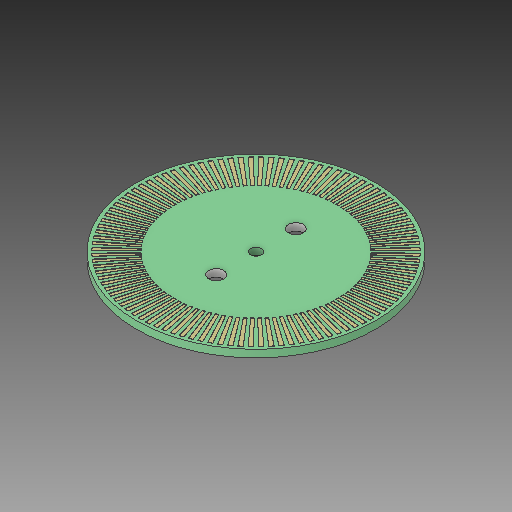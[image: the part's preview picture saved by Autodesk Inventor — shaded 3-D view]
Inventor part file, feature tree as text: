
AUTODESK INVENTOR PART (.ipt)
format: ipt  version: 2018.2 (Build 222227000, 227)  size: 907,264 bytes
history: native  units: mm
features: sketch x3, extrude x2, pattern_circular x1, plane x1, mirror x1, hole x1
ambient origin geometry x8: Origin, YZ Plane, XZ Plane, XY Plane, X Axis, Y Axis, Z Axis, Center Point
bodies: Solid1 (feature_tree)
feature tree (9):
  extrude  "Extrusion1"  Depth=2.23mm
  extrude  "Extrusion2"  Depth=1.5mm
  pattern_circular  "Circular Pattern1"  [2 undecoded]
  plane  "Work Plane1"
  mirror  "Mirror1"
  hole  "Hole1"  [1 undecoded]
  sketch  "Sketch1"  dims[d0=48.0mm d1=2.23mm]
  sketch  "Sketch2"  dims[d2=1.5mm d3=0.0mm d4=0.7mm]
  sketch  "Sketch3"  dims[d5=7.0mm d6=0.75mm d7=0.1mm d8=0.0mm d9=1000.0mm d10=360.0deg d12=0.524678mm d13=8.0mm d14=8.0mm d15=3.0mm d16=6.0mm d17=4.0mm d18=2.0mm d19=90.0deg d20=8.0mm d21=20.594885mm]
note: 3 required parameter values undecoded (feature->parameter linkage not recoverable at this tier; creation-order binding heuristic only, values carry confidence <= 0.55)
